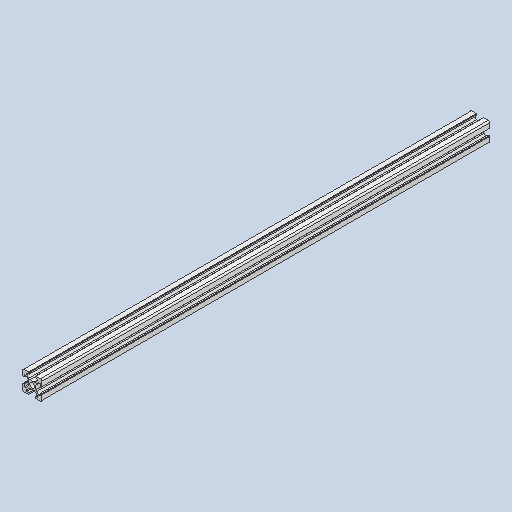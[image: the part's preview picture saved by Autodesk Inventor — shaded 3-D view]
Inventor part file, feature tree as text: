
AUTODESK INVENTOR PART (.ipt)
format: ipt  version: 2023 (Build 270158000, 158)  size: 261,120 bytes
history: native  units: mm
features: extrude x1, sketch x1, projected_geometry x1
ambient origin geometry x8: Origin, YZ Plane, XZ Plane, XY Plane, X Axis, Y Axis, Z Axis, Center Point
bodies: Solid1 (feature_tree), Body1 (feature_tree)
feature tree (3):
  extrude  "Extrusion1"  [1 undecoded]
  sketch  "Sketch1"  dims[d0=360.0mm d1=0.0mm]
  projected_geometry  "Projected Loop1"
note: 1 required parameter value undecoded (feature->parameter linkage not recoverable at this tier; creation-order binding heuristic only, values carry confidence <= 0.55)
